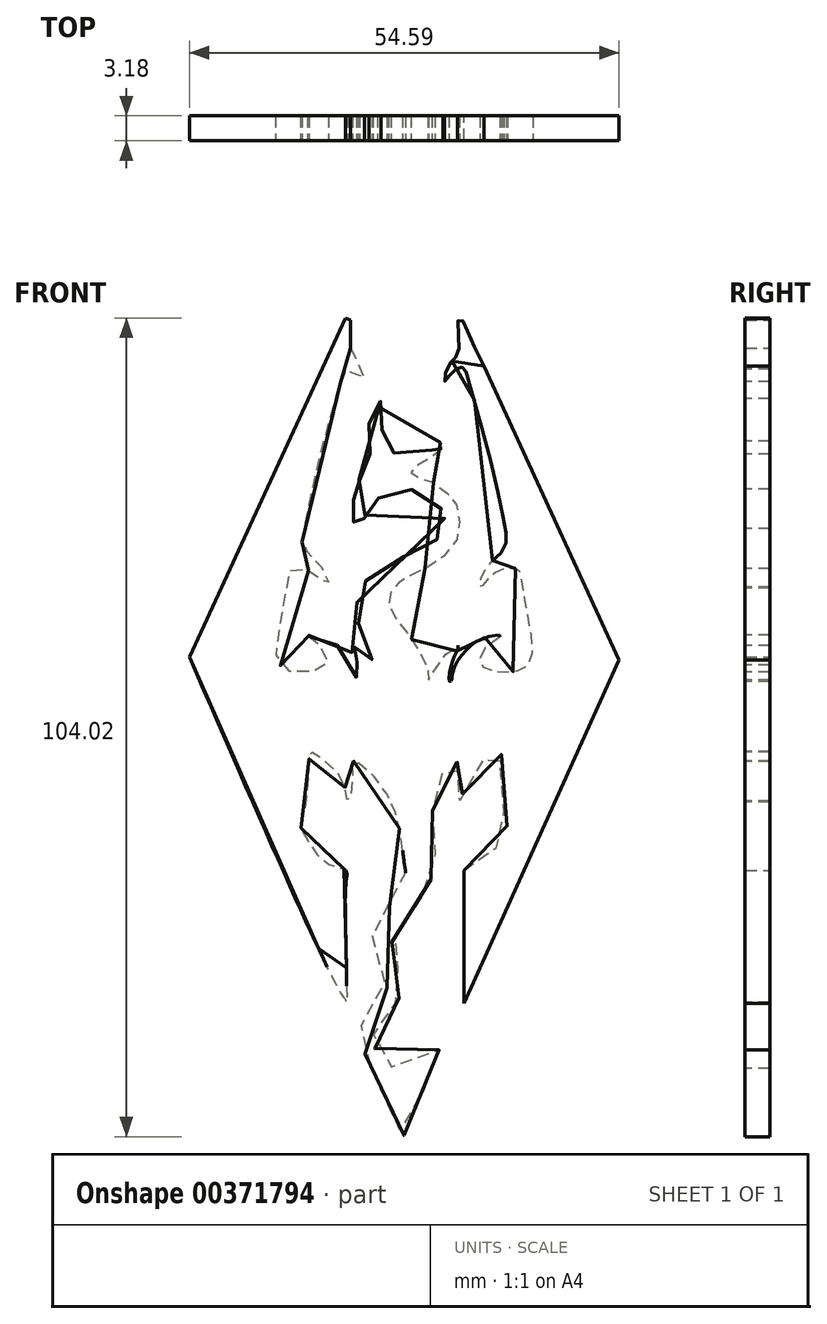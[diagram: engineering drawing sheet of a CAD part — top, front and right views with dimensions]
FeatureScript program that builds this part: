
annotation { "Feature Type Name" : "Feature", "Feature Type Description" : "" }
export const myFeature = defineFeature(function(context is Context, id is Id, definition is map)
    precondition{}
    {
        {
            var Q0;
            Q0=qCreatedBy(makeId("Front.planeOp"),FACE);
            var sketch = newSketch(context, id + "F0", { "sketchPlane" : qUnion([Q0])});
            skLineSegment(sketch, "E0", {"start": v(-21.05, 16.65) * mm, "end": v(-1.24, 59.75) * mm});
            skLineSegment(sketch, "E1", {"start": v(-1.24, 59.75) * mm, "end": v(-0.56, 59.44) * mm});
            skLineSegment(sketch, "E2", {"start": v(-0.56, 59.44) * mm, "end": v(-0.56, 55.89) * mm});
            skFitSpline(sketch, "E3", {"points": [v(-0.56, 55.89) * mm, v(-0.2, 55) * mm, v(0.54, 53.8) * mm, v(1.12, 52.52) * mm, v(1.08, 51.68) * mm, v(0.68, 52.03) * mm, v(0.01, 52.92) * mm, v(-1, 53.23) * mm, v(-1.85, 51.63) * mm, v(-3.27, 46.8) * mm, v(-5.26, 39) * mm, v(-6.63, 32.23) * mm, v(-6.72, 30.99) * mm, v(-6.15, 30.06) * mm, v(-4.68, 28.55) * mm, v(-3.75, 27.36) * mm, v(-3.35, 25.98) * mm, v(-3.44, 25.54) * mm, v(-3.93, 26.25) * mm, v(-5.57, 27.53) * mm, v(-7.74, 27.89) * mm, v(-8.32, 27.53) * mm, v(-8.67, 26.03) * mm, v(-9.75, 19.7) * mm, v(-10.07, 16.91) * mm, v(-8.9, 15.07) * mm, v(-6.06, 14.8) * mm, v(-4.06, 15.23) * mm, v(-3.38, 16.33) * mm, v(-4.27, 17.91) * mm, v(-5.54, 19.02) * mm, v(-6, 19.33) * mm, v(-5.11, 19.44) * mm, v(-2.22, 18.12) * mm, v(-0.06, 15.23) * mm, v(0.31, 13.6) * mm, v(0.48, 13.74) * mm, v(0.35, 15.7) * mm, v(-0.67, 17.78) * mm, v(-0.68, 18.04) * mm, v(-0.16, 18) * mm, v(2.18, 15.62) * mm, v(2.26, 15.8) * mm, v(1.5, 17.93) * mm, v(0.3, 21.47) * mm, v(0.97, 25.84) * mm, v(5.03, 29) * mm, v(8.05, 30.03) * mm, v(10.7, 31.93) * mm, v(11.36, 34.34) * mm, v(10.12, 36.53) * mm, v(7.38, 37.91) * mm, v(4.58, 37.69) * mm, v(2.52, 36.46) * mm, v(1.5, 35.36) * mm, v(1.14, 34.04) * mm, v(0.93, 33.01) * mm, v(0.28, 33.31) * mm, v(-0.43, 34.17) * mm, v(-0.72, 35.55) * mm, v(-0.13, 36.65) * mm, v(0.34, 37.22) * mm, v(0.56, 37.95) * mm, v(0.52, 39.44) * mm, v(0.63, 39.94) * mm, v(2, 42.75) * mm, v(2.06, 44.17) * mm, v(1.88, 47.21) * mm, v(3.16, 49.5) * mm, v(3.25, 49.09) * mm, v(2.85, 47.35) * mm, v(3.6, 45.09) * mm, v(4.23, 43.27) * mm, v(4.93, 42.6) * mm, v(8.63, 42.61) * mm, v(10.48, 43.44) * mm, v(11.06, 44.07) * mm, v(11.11, 43.3) * mm, v(10.58, 42.66) * mm, v(8.57, 41.36) * mm, v(7.33, 40.58) * mm, v(7.1, 40) * mm, v(7.73, 39.52) * mm, v(9.05, 39.25) * mm, v(11.34, 37.81) * mm, v(12.78, 36.3) * mm, v(13.26, 33.83) * mm, v(12.78, 31.26) * mm, v(10.07, 28.5) * mm, v(8.04, 27.54) * mm, v(5.86, 26.34) * mm, v(4.82, 25.41) * mm, v(4.33, 24.22) * mm, v(4.42, 22.71) * mm, v(5.8, 20.8) * mm, v(8.05, 17.57) * mm, v(9.29, 14.95) * mm, v(9.34, 13.8) * mm, v(9.65, 13.8) * mm, v(9.91, 14.85) * mm, v(12.84, 18.09) * mm, v(13.1, 18.09) * mm, v(12.75, 17.03) * mm, v(12.17, 15.39) * mm, v(11.95, 13.57) * mm, v(12.13, 13.57) * mm, v(12.3, 13.88) * mm, v(12.44, 14.9) * mm, v(14.08, 17.51) * mm, v(16.65, 19.15) * mm, v(18.42, 19.37) * mm, v(18.02, 18.89) * mm, v(16.91, 18.18) * mm, v(15.9, 16.54) * mm, v(16.3, 15.34) * mm, v(18.24, 14.81) * mm, v(20.51, 14.9) * mm, v(22.27, 15.96) * mm, v(22.3, 20.03) * mm, v(21.33, 25.3) * mm, v(20.92, 27.52) * mm, v(20.54, 27.83) * mm, v(19.38, 27.92) * mm, v(18.07, 27.52) * mm, v(16.78, 26.51) * mm, v(16.16, 25.73) * mm, v(15.94, 25.42) * mm, v(15.84, 26.01) * mm, v(16.22, 27.14) * mm, v(17.13, 28.58) * mm, v(18.38, 29.74) * mm, v(19.2, 31.15) * mm, v(19.13, 32.68) * mm, v(17.65, 39.84) * mm, v(14.14, 52.74) * mm, v(13.82, 53.37) * mm, v(13.47, 53.49) * mm, v(12.92, 53.28) * mm, v(12.25, 52.72) * mm, v(11.5, 51.7) * mm, v(11.4, 51.7) * mm, v(11.4, 52.47) * mm, v(12.1, 54.03) * mm, v(12.56, 54.5) * mm, v(13.07, 55.4) * mm, v(13.18, 56.98) * mm, v(13.17, 59.6) * mm, v(13.65, 59.46) * mm, v(14.28, 58.04) * mm, v(16.4, 53.6) * mm], "startDerivative": vector(57.6, -172.42) * mm, "endDerivative": vector(223.02, -434.4) * mm});
            skLineSegment(sketch, "E4", {"start": v(16.4, 53.6) * mm, "end": v(33.54, 16.28) * mm});
            skLineSegment(sketch, "E5", {"start": v(33.54, 16.28) * mm, "end": v(13.82, -27.35) * mm});
            skLineSegment(sketch, "E6", {"start": v(13.82, -27.35) * mm, "end": v(13.82, -10.44) * mm});
            skFitSpline(sketch, "E7", {"points": [v(13.82, -10.44) * mm, v(15.36, -9.77) * mm, v(17.82, -7.68) * mm, v(19.32, -5.4) * mm, v(18.97, -3.36) * mm, v(18.88, -1.37) * mm, v(18.44, 3.82) * mm, v(18.64, 4.54) * mm, v(18.34, 4.54) * mm, v(16.25, 3.57) * mm, v(14.4, 1.11) * mm, v(13.2, -1.65) * mm, v(13.05, -0.3) * mm, v(12.9, 1.11) * mm, v(13.12, 3.35) * mm, v(12.94, 3.32) * mm, v(11.9, 2.6) * mm, v(10.36, 0.84) * mm, v(9.84, -0.79) * mm, v(9.89, -3.92) * mm, v(10.07, -6.93) * mm, v(10.12, -9.98) * mm, v(9.19, -12.48) * mm, v(6.76, -16.43) * mm, v(5.04, -18.9) * mm, v(4.63, -19.75) * mm, v(4.7, -20.72) * mm, v(5.85, -24.54) * mm, v(5.95, -25.86) * mm, v(4.97, -27.46) * mm, v(3.27, -29.82) * mm, v(2.42, -31.03) * mm, v(2.37, -32.61) * mm, v(3.95, -34.98) * mm, v(6.95, -35.4) * mm, v(10.75, -33.24) * mm, v(11, -33.35) * mm, v(9.59, -36.4) * mm, v(6.06, -44.26) * mm, v(5.74, -43.52) * mm, v(2.95, -37.51) * mm, v(0.47, -31.87) * mm, v(0.47, -30.77) * mm, v(3.9, -25.76) * mm, v(4, -25.18) * mm, v(1.74, -20.02) * mm, v(2.1, -18.91) * mm, v(6.27, -11.22) * mm, v(6.32, -9.96) * mm, v(5.9, -6.59) * mm, v(4.87, -2.4) * mm, v(1.86, 2.03) * mm, v(-0.26, 3.45) * mm, v(-0.35, 3.1) * mm, v(-0.54, -1.12) * mm, v(-0.93, -1.74) * mm, v(-1.17, -0.42) * mm, v(-2.17, 1.93) * mm, v(-4.85, 4.16) * mm, v(-5.79, 4.65) * mm, v(-5.82, 3.9) * mm, v(-6.08, -0.05) * mm, v(-6.57, -3.47) * mm, v(-6.9, -4.85) * mm, v(-6.64, -5.52) * mm, v(-5.41, -7.6) * mm, v(-3.36, -9.66) * mm, v(-1.2, -10.44) * mm, v(-1.13, -11.82) * mm, v(-1.2, -17.33) * mm, v(-1.08, -27.23) * mm, v(-1.16, -27.01) * mm, v(-1.9, -25.82) * mm, v(-21.05, 16.65) * mm], "startDerivative": vector(136.02, 46.02) * mm, "endDerivative": vector(-436.92, 1003.69) * mm});
            skSolve(sketch);
        }
        {
            var Q0;
            Q0=qSketchRegion(id+"F0",true);
            extrude(context, id + "F1", {"entities" : qUnion([Q0]), "depth" : 3.17 * mm});
        }
    });
